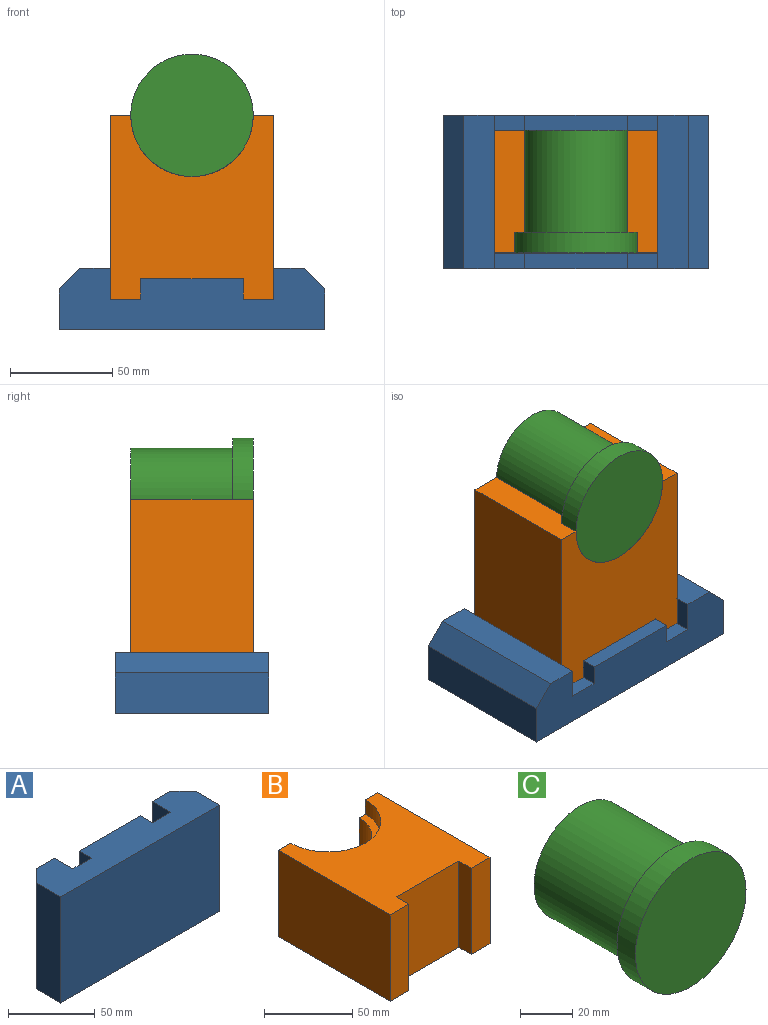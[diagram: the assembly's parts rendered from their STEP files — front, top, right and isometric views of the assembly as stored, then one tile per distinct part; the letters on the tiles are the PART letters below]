
ASSEMBLY  parts=3 mates=2
PART A: 16 faces, bbox 130x30x75 mm
  f0: plane 75x15mm, normal (0,1,0), area 1125mm2, adj f1,f13,f14,f15
  f1: plane 75x15mm, normal (-1,0,0), area 1125mm2, adj f0,f2,f14,f15
  f2: plane 75x15mm, normal (0,1,0), area 1125mm2, adj f1,f3,f14,f15
  f3: plane 75x10mm, normal (1,0,0), area 750mm2, adj f2,f4,f14,f15
  f4: plane 75x50mm, normal (0,1,0), area 3750mm2, adj f3,f5,f14,f15
  f5: plane 75x10mm, normal (-1,0,0), area 750mm2, adj f4,f6,f14,f15
  f6: plane 75x15mm, normal (0,1,0), area 1125mm2, adj f5,f7,f14,f15
  f7: plane 75x15mm, normal (1,0,0), area 1125mm2, adj f6,f8,f14,f15
  f8: plane 75x15mm, normal (0,1,0), area 1125mm2, adj f7,f9,f14,f15
  f9: plane 75x10mm, normal (-0.71,0.71,0), area 1060.7mm2, adj f8,f10,f14,f15
  f10: plane 75x20mm, normal (-1,0,0), area 1500mm2, adj f9,f11,f14,f15
  f11: plane 130x75mm, normal (0,-1,0), area 9750mm2, adj f10,f12,f14,f15
  f12: plane 75x20mm, normal (1,0,0), area 1500mm2, adj f11,f13,f14,f15
  f13: plane 75x10mm, normal (0.71,0.71,0), area 1060.7mm2, adj f0,f12,f14,f15
  f14: plane 130x30mm, normal (0,0,1), area 3100mm2, adj f0,f1,f2,f3,f4,f5,f6,f7
  f15: plane 130x30mm, normal (0,0,-1), area 3100mm2, adj f0,f1,f2,f3,f4,f5,f6,f7
PART B: 14 faces, bbox 80x90x60 mm
  f0: plane 60x15mm, normal (0,1,0), area 850mm2, adj f2,f5,f10,f11,f12,f13
  f1: plane 60x15mm, normal (0,1,0), area 850mm2, adj f2,f6,f10,f11,f12,f13
  f2: plane 90x80mm, normal (0,0,-1), area 5718.3mm2, adj f0,f1,f3,f4,f5,f6,f7,f8
  f3: plane 60x10mm, normal (-1,0,0), area 600mm2, adj f2,f4,f9,f10
  f4: plane 60x15mm, normal (0,-1,0), area 900mm2, adj f2,f3,f5,f10
  f5: plane 90x60mm, normal (1,0,0), area 5400mm2, adj f0,f2,f4,f10
  f6: plane 90x60mm, normal (-1,0,0), area 5400mm2, adj f1,f2,f7,f10
  f7: plane 60x15mm, normal (0,-1,0), area 900mm2, adj f2,f6,f8,f10
  f8: plane 60x10mm, normal (1,0,0), area 600mm2, adj f2,f7,f9,f10
  f9: plane 60x50mm, normal (0,-1,0), area 3000mm2, adj f2,f3,f8,f10
  f10: plane 90x80mm, normal (0,0,1), area 5286.3mm2, adj f0,f1,f3,f4,f5,f6,f7,f8
  f11: cylinder r=25mm len=50mm, axis (0,0,-1), area 3927mm2, adj f0,f1,f2,f12
  f12: plane 60x30mm, normal (0,0,1), area 432mm2, adj f0,f1,f11,f13
  f13: cylinder r=30mm len=60mm, axis (0,0,1), area 942.5mm2, adj f0,f1,f10,f12
PART C: 5 faces, bbox 60x60x60 mm
  f0: cylinder r=30mm len=60mm, axis (0,1,0), area 1885mm2, adj f1,f2
  f1: plane 60x60mm, normal (0,-1,0), area 2827.4mm2, adj f0
  f2: plane 60x60mm, normal (0,1,0), area 863.9mm2, adj f0,f3
  f3: cylinder r=25mm len=50mm, axis (0,-1,0), area 7854mm2, adj f2,f4
  f4: plane 50x50mm, normal (0,1,0), area 1963.5mm2, adj f3
PLACE A rot(axis=(1,0,0),90deg) t=(-53.73,65.18,-132.55)mm
PLACE B rot(axis=(1,0,0),90deg) t=(-53.73,57.68,-87.55)mm
PLACE C t=(-53.73,7.68,-42.55)mm
MATE fastened A.f4 <-> B.f9  axis (0,0,1) through (-53.73,27.68,-122.55)mm
MATE fastened B.f11 <-> C.f3  axis (0,1,0) through (-53.73,57.68,-42.55)mm
